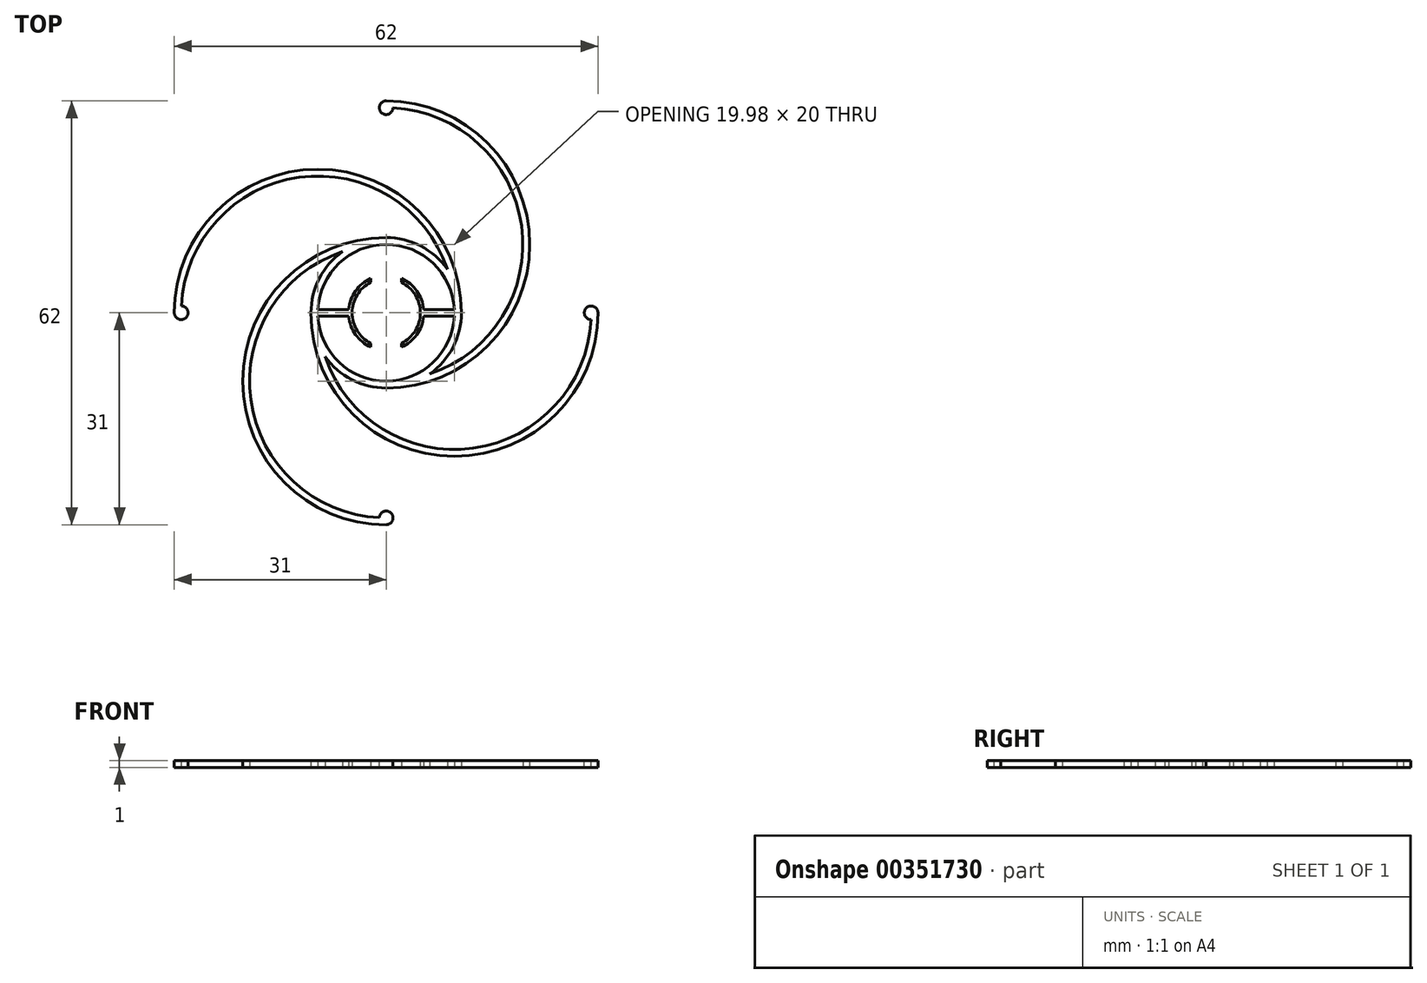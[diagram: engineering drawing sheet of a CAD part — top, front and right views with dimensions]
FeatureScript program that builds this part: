
annotation { "Feature Type Name" : "Feature", "Feature Type Description" : "" }
export const myFeature = defineFeature(function(context is Context, id is Id, definition is map)
    precondition{}
    {
        {
            var Q0;
            Q0=qCreatedBy(makeId("Top.planeOp"),FACE);
            var sketch = newSketch(context, id + "F0", { "sketchPlane" : qUnion([Q0])});
            skCircle(sketch, "E0", {"center": v(0, 0) * mm, "radius": 10 * mm});
            skPoint(sketch, "E1", {"position": v(10, 0) * mm});
            skArc(sketch, "E2", {"start": v(10, 0) * mm, "mid": v(-10, 20) * mm, "end": v(-30, 0) * mm});
            skArc(sketch, "E3.1.0", {"start": v(0, 10) * mm, "mid": v(-20, -10) * mm, "end": v(0, -30) * mm});
            skArc(sketch, "E3.2.0", {"start": v(-10, 0) * mm, "mid": v(10, -20) * mm, "end": v(30, 0) * mm});
            skArc(sketch, "E3.3.0", {"start": v(0, -10) * mm, "mid": v(20, 10) * mm, "end": v(0, 30) * mm});
            skArc(sketch, "E4.0", {"start": v(11, 0) * mm, "mid": v(-10, 21) * mm, "end": v(-31, 0) * mm});
            skArc(sketch, "E5.0", {"start": v(0, -11) * mm, "mid": v(21, 10) * mm, "end": v(0, 31) * mm});
            skArc(sketch, "E6.0", {"start": v(-11, 0) * mm, "mid": v(10, -21) * mm, "end": v(31, 0) * mm});
            skArc(sketch, "E7.0", {"start": v(0, 11) * mm, "mid": v(-21, -10) * mm, "end": v(0, -31) * mm});
            skCircle(sketch, "E8.0", {"center": v(0, 0) * mm, "radius": 11 * mm});
            skLineSegment(sketch, "E9", {"start": v(-31, 0) * mm, "end": v(-30, 0) * mm});
            skLineSegment(sketch, "E10.1.0", {"start": v(0, -31) * mm, "end": v(0, -30) * mm});
            skLineSegment(sketch, "E10.2.0", {"start": v(31, 0) * mm, "end": v(30, 0) * mm});
            skLineSegment(sketch, "E10.3.0", {"start": v(0, 31) * mm, "end": v(0, 30) * mm});
            skCircle(sketch, "E11", {"center": v(0, 0) * mm, "radius": 5 * mm});
            skLineSegment(sketch, "E12.bottom", {"start": v(-2.25, 6.35) * mm, "end": v(2.25, 6.35) * mm});
            skLineSegment(sketch, "E12.top", {"start": v(-2.25, -6.35) * mm, "end": v(2.25, -6.35) * mm});
            skLineSegment(sketch, "E12.left", {"start": v(-2.25, 6.35) * mm, "end": v(-2.25, -6.35) * mm});
            skLineSegment(sketch, "E12.right", {"start": v(2.25, 6.35) * mm, "end": v(2.25, -6.35) * mm});
            skCircle(sketch, "E13", {"center": v(0, 0) * mm, "radius": 5.5 * mm});
            skLineSegment(sketch, "E14.0.left", {"start": v(5.48, 0.5) * mm, "end": v(9.99, 0.5) * mm});
            skLineSegment(sketch, "E14.0.right", {"start": v(5.48, -0.5) * mm, "end": v(9.99, -0.5) * mm});
            skLineSegment(sketch, "E15.0.left", {"start": v(-9.99, 0.5) * mm, "end": v(-5.48, 0.5) * mm});
            skLineSegment(sketch, "E15.0.right", {"start": v(-9.99, -0.5) * mm, "end": v(-5.48, -0.5) * mm});
            skSolve(sketch);
        }
        {
            var Q0;
            Q0 = qSketchRegion(id + "F0", true);
            var Q1;
            {var subQ0=sQuery(id+"F0.wireOp",EDGE,"E12.right");var subQ1=sQuery(id+"F0.wireOp",EDGE,"E11");var subQ2=makeQuery(id+"F0.imprint","INTERSECT",VERTEX,{"disambiguationData":[OD(0.0)],"derivedFrom":[subQ1,subQ0]});Q1=makeQuery(id+"F0.imprint","IMPRINT",FACE,{"disambiguationData":[TD([[makeQuery(id+"F0.imprint","IMPRINT",EDGE,{"disambiguationData":[TD([[subQ2,1.0]])],"derivedFrom":subQ1}),-1.0]])]});}
            var Q2;
            {var subQ0=sQuery(id+"F0.wireOp",EDGE,"E13");var subQ1=makeQuery(id+"F0.imprint","INTERSECT",VERTEX,{"derivedFrom":[subQ0,sQuery(id+"F0.wireOp",EDGE,"HZhyL7h6-VQSw-KTV3-gyIE-tWRtW2MqsSft")]});Q2=makeQuery(id+"F0.imprint","IMPRINT",FACE,{"disambiguationData":[TD([[makeQuery(id+"F0.imprint","IMPRINT",EDGE,{"disambiguationData":[TD([[subQ1,1.0]])],"derivedFrom":subQ0}),1.0]])]});}
            var Q3;
            {var subQ0=sQuery(id+"F0.wireOp",EDGE,"HZhyL7h6-VQSw-KTV3-gyIE-tWRtW2MqsSft");Q3=makeQuery(id+"F0.imprint","IMPRINT",FACE,{"disambiguationData":[TD([[makeQuery(id+"F0.imprint","IMPRINT",EDGE,{"derivedFrom":subQ0}),-1.0]])]});}
            var Q4;
            {var subQ0=sQuery(id+"F0.wireOp",EDGE,"qH6tGRLT-AlYr-FnlA-XhZf-ETqYmGUl5ZGN");Q4=makeQuery(id+"F0.imprint","IMPRINT",FACE,{"disambiguationData":[TD([[makeQuery(id+"F0.imprint","IMPRINT",EDGE,{"derivedFrom":subQ0}),1.0]])]});}
            var Q5;
            {var subQ0=sQuery(id+"F0.wireOp",EDGE,"qH6tGRLT-AlYr-FnlA-XhZf-ETqYmGUl5ZGN");Q5=makeQuery(id+"F0.imprint","IMPRINT",FACE,{"disambiguationData":[TD([[makeQuery(id+"F0.imprint","IMPRINT",EDGE,{"derivedFrom":subQ0}),-1.0]])]});}
            var Q6;
            {var subQ0=sQuery(id+"F0.wireOp",EDGE,"E14.0.left");Q6=makeQuery(id+"F0.imprint","IMPRINT",FACE,{"disambiguationData":[TD([[makeQuery(id+"F0.imprint","IMPRINT",EDGE,{"derivedFrom":subQ0}),-1.0]])]});}
            var Q7;
            {var subQ2=sQuery(id+"F0.wireOp",EDGE,"E12.left");var subQ4=sQuery(id+"F0.wireOp",EDGE,"E11");var subQ5=makeQuery(id+"F0.imprint","INTERSECT",VERTEX,{"disambiguationData":[OD(0.0)],"derivedFrom":[subQ4,subQ2]});Q7=makeQuery(id+"F0.imprint","IMPRINT",FACE,{"disambiguationData":[TD([[makeQuery(id+"F0.imprint","IMPRINT",EDGE,{"disambiguationData":[TD([[subQ5,-1.0]])],"derivedFrom":subQ4}),-1.0]])]});}
            var Q8;
            {var subQ0=sQuery(id+"F0.wireOp",EDGE,"E15.0.left");Q8=makeQuery(id+"F0.imprint","IMPRINT",FACE,{"disambiguationData":[TD([[makeQuery(id+"F0.imprint","IMPRINT",EDGE,{"derivedFrom":subQ0}),-1.0]])]});}
            extrude(context, id + "F1", {"entities" : qUnion([Q0, Q1, Q2, Q3, Q4, Q5, Q6, Q7, Q8]), "depth" : 1 * mm});
        }
        {
            var Q0;
            Q0=makeQuery(id+"F1.opExtrude","SWEPT_FACE",FACE,{"disambiguationData":[OSD([sQuery(id+"F0.wireOp",EDGE,"E9")])]});
            var Q1;
            Q1=makeQuery(id+"F1.opExtrude","SWEPT_EDGE",EDGE,{"disambiguationData":[OSD([sQuery(id+"F0.wireOp",EDGE,"E2"),sQuery(id+"F0.wireOp",EDGE,"E9")])]});
            revolve(context, id + "F2", {"operationType" : NewBodyOperationType.ADD, "entities" : qUnion([Q0]), "axis" : qUnion([Q1]), "revolveType" : RevolveType.FULL});
        }
        {
            var Q0;
            Q0=makeQuery(id+"F1.opExtrude","SWEPT_FACE",FACE,{"disambiguationData":[OSD([sQuery(id+"F0.wireOp",EDGE,"E10.1.0")])]});
            var Q1;
            Q1=makeQuery(id+"F1.opExtrude","SWEPT_EDGE",EDGE,{"disambiguationData":[OSD([sQuery(id+"F0.wireOp",EDGE,"E3.1.0"),sQuery(id+"F0.wireOp",EDGE,"E10.1.0")])]});
            revolve(context, id + "F3", {"operationType" : NewBodyOperationType.ADD, "entities" : qUnion([Q0]), "axis" : qUnion([Q1]), "revolveType" : RevolveType.FULL});
        }
        {
            var Q0;
            Q0=makeQuery(id+"F1.opExtrude","SWEPT_FACE",FACE,{"disambiguationData":[OSD([sQuery(id+"F0.wireOp",EDGE,"E10.2.0")])]});
            var Q1;
            Q1=makeQuery(id+"F1.opExtrude","SWEPT_EDGE",EDGE,{"disambiguationData":[OSD([sQuery(id+"F0.wireOp",EDGE,"E3.2.0"),sQuery(id+"F0.wireOp",EDGE,"E10.2.0")])]});
            revolve(context, id + "F4", {"operationType" : NewBodyOperationType.ADD, "entities" : qUnion([Q0]), "axis" : qUnion([Q1]), "revolveType" : RevolveType.FULL});
        }
        {
            var Q0;
            Q0=makeQuery(id+"F1.opExtrude","SWEPT_FACE",FACE,{"disambiguationData":[OSD([sQuery(id+"F0.wireOp",EDGE,"E10.3.0")])]});
            var Q1;
            Q1=makeQuery(id+"F1.opExtrude","SWEPT_EDGE",EDGE,{"disambiguationData":[OSD([sQuery(id+"F0.wireOp",EDGE,"E3.3.0"),sQuery(id+"F0.wireOp",EDGE,"E10.3.0")])]});
            revolve(context, id + "F5", {"operationType" : NewBodyOperationType.ADD, "entities" : qUnion([Q0]), "axis" : qUnion([Q1]), "revolveType" : RevolveType.FULL});
        }
    });
